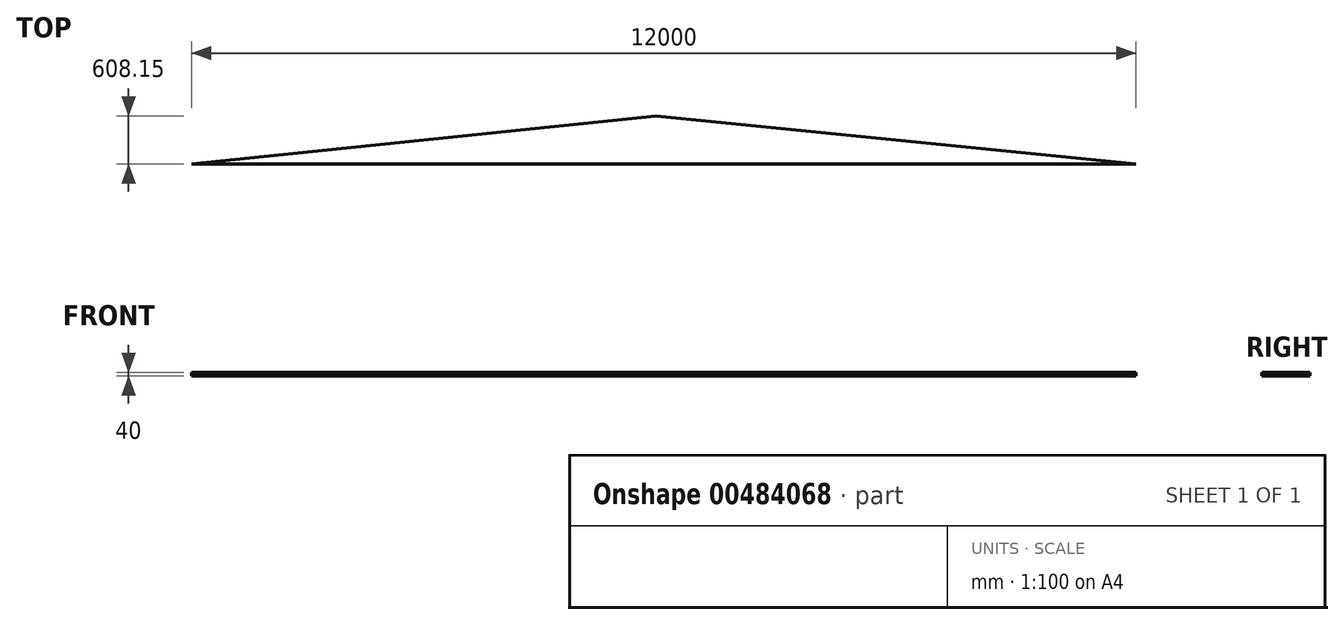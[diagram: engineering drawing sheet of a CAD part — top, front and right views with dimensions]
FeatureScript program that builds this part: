
annotation { "Feature Type Name" : "Feature", "Feature Type Description" : "" }
export const myFeature = defineFeature(function(context is Context, id is Id, definition is map)
    precondition{}
    {
        {
            var Q0;
            Q0=qCreatedBy(makeId("Top.planeOp"),FACE);
            var sketch = newSketch(context, id + "F0", { "sketchPlane" : qUnion([Q0])});
            skLineSegment(sketch, "E0", {"start": v(0, 0) * mm, "end": v(12000, 0) * mm});
            skLineSegment(sketch, "E1", {"start": v(6000, 0) * mm, "end": v(5899.43, 608.15) * mm});
            skLineSegment(sketch, "E2", {"start": v(5899.43, 608.15) * mm, "end": v(0, 0) * mm});
            skLineSegment(sketch, "E3", {"start": v(5899.43, 608.15) * mm, "end": v(12000, 0) * mm});
            skSolve(sketch);
        }
        {
            var Q0;
            Q0 = qSketchRegion(id + "F0", true);
            extrude(context, id + "F1", {"entities" : qUnion([Q0]), "depth" : 40 * mm, "offsetDistance" : 25 * mm});
        }
    });
